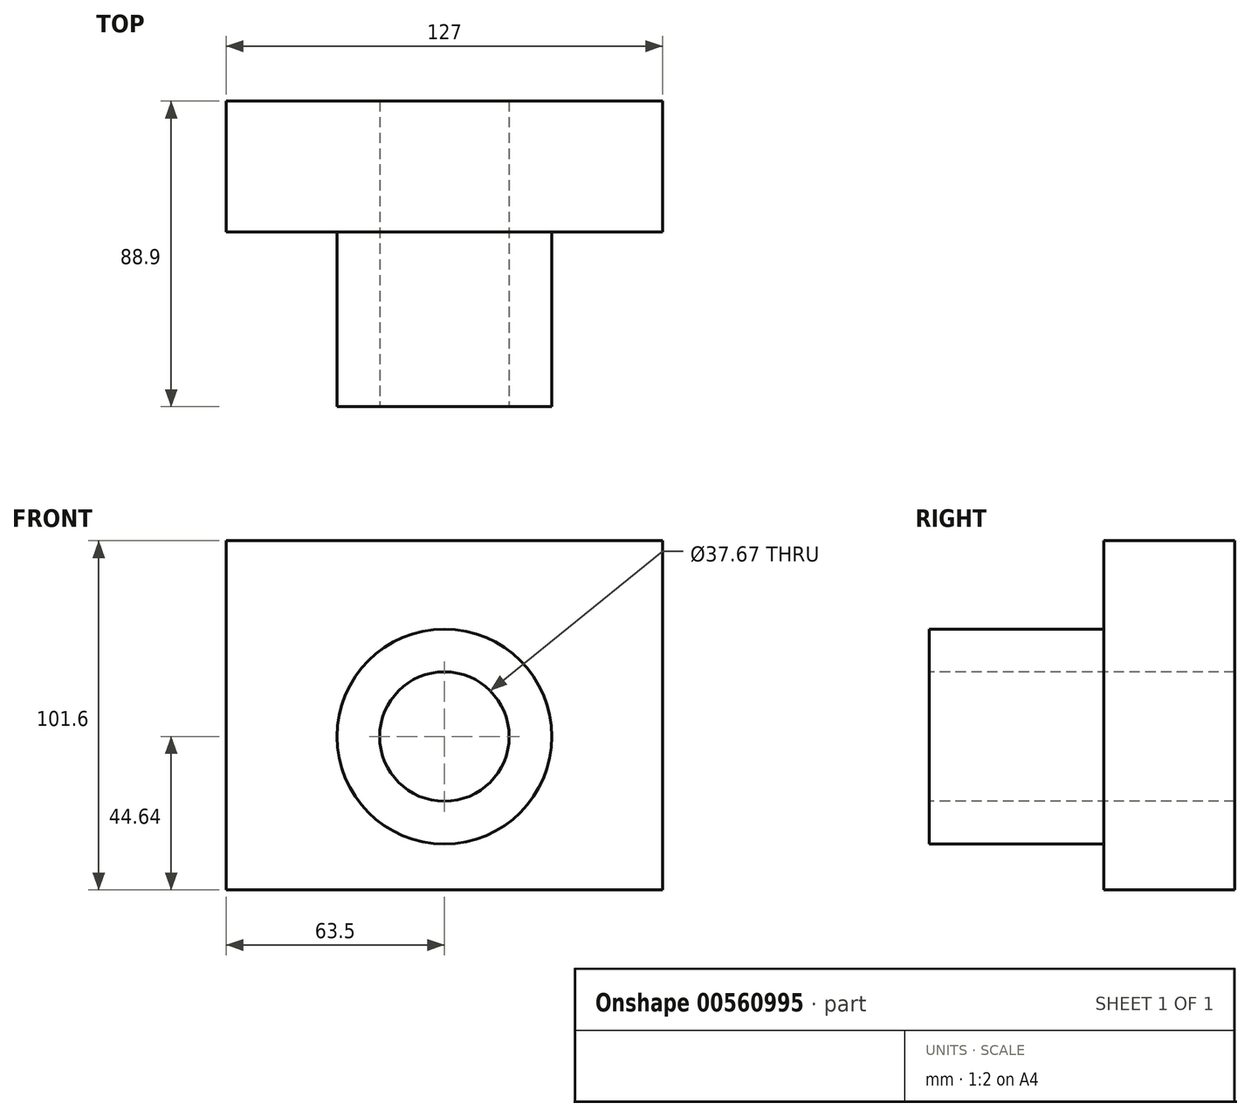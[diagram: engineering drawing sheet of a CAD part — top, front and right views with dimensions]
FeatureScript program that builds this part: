
annotation { "Feature Type Name" : "Feature", "Feature Type Description" : "" }
export const myFeature = defineFeature(function(context is Context, id is Id, definition is map)
    precondition{}
    {
        {
            var Q0;
            Q0=qCreatedBy(makeId("Front.planeOp"),FACE);
            var sketch = newSketch(context, id + "F0", { "sketchPlane" : qUnion([Q0])});
            skLineSegment(sketch, "E0.bottom", {"start": v(63.5, 50.8) * mm, "end": v(-63.5, 50.8) * mm});
            skLineSegment(sketch, "E0.top", {"start": v(63.5, -50.8) * mm, "end": v(-63.5, -50.8) * mm});
            skLineSegment(sketch, "E0.left", {"start": v(63.5, 50.8) * mm, "end": v(63.5, -50.8) * mm});
            skLineSegment(sketch, "E0.right", {"start": v(-63.5, 50.8) * mm, "end": v(-63.5, -50.8) * mm});
            skPoint(sketch, "E0.middle", {"position": v(0, 0) * mm});
            skSolve(sketch);
        }
        {
            var Q0;
            Q0=makeQuery(id+"F0.imprint","IMPRINT",FACE,{"disambiguationData":[TD([[makeQuery(id+"F0.imprint","IMPRINT",EDGE,{"derivedFrom":sQuery(id+"F0.wireOp",EDGE,"E0.bottom")}),1.0]])]});
            extrude(context, id + "F1", {"entities" : qUnion([Q0]), "depth" : 38.1 * mm, "offsetDistance" : 25.4 * mm});
        }
        {
            var Q0;
            Q0=makeQuery(id+"F1.opExtrude","CAP_FACE",FACE,{"disambiguationData":[OSD([sQuery(id+"F0.wireOp",EDGE,"E0.bottom"),sQuery(id+"F0.wireOp",EDGE,"E0.top"),sQuery(id+"F0.wireOp",EDGE,"E0.left"),sQuery(id+"F0.wireOp",EDGE,"E0.right")])],"isStart":false});
            var sketch = newSketch(context, id + "F2", { "sketchPlane" : qUnion([Q0])});
            skCircle(sketch, "E1", {"center": v(0, -6.16) * mm, "radius": 31.25 * mm});
            skSolve(sketch);
        }
        {
            var Q0;
            Q0=makeQuery(id+"F2.imprint","IMPRINT",FACE,{"disambiguationData":[TD([[makeQuery(id+"F2.imprint","IMPRINT",EDGE,{"derivedFrom":sQuery(id+"F2.wireOp",EDGE,"E1")}),1.0]])]});
            extrude(context, id + "F3", {"entities" : qUnion([Q0]), "operationType" : NewBodyOperationType.ADD, "depth" : 50.8 * mm, "offsetDistance" : 25.4 * mm});
        }
        {
            var Q0;
            Q0=makeQuery(id+"F3.opExtrude","CAP_FACE",FACE,{"disambiguationData":[OSD([sQuery(id+"F2.wireOp",EDGE,"E1")])],"isStart":false});
            var sketch = newSketch(context, id + "F4", { "sketchPlane" : qUnion([Q0])});
            skCircle(sketch, "E2", {"center": v(0, -6.16) * mm, "radius": 18.84 * mm});
            skSolve(sketch);
        }
        {
            var Q0;
            Q0=makeQuery(id+"F4.imprint","IMPRINT",FACE,{"disambiguationData":[TD([[makeQuery(id+"F4.imprint","IMPRINT",EDGE,{"derivedFrom":sQuery(id+"F4.wireOp",EDGE,"E2")}),1.0]])]});
            extrude(context, id + "F5", {"entities" : qUnion([Q0]), "operationType" : NewBodyOperationType.REMOVE, "endBound" : BoundingType.THROUGH_ALL, "oppositeDirection" : true, "depth" : 25.4 * mm, "offsetDistance" : 25.4 * mm});
        }
    });
